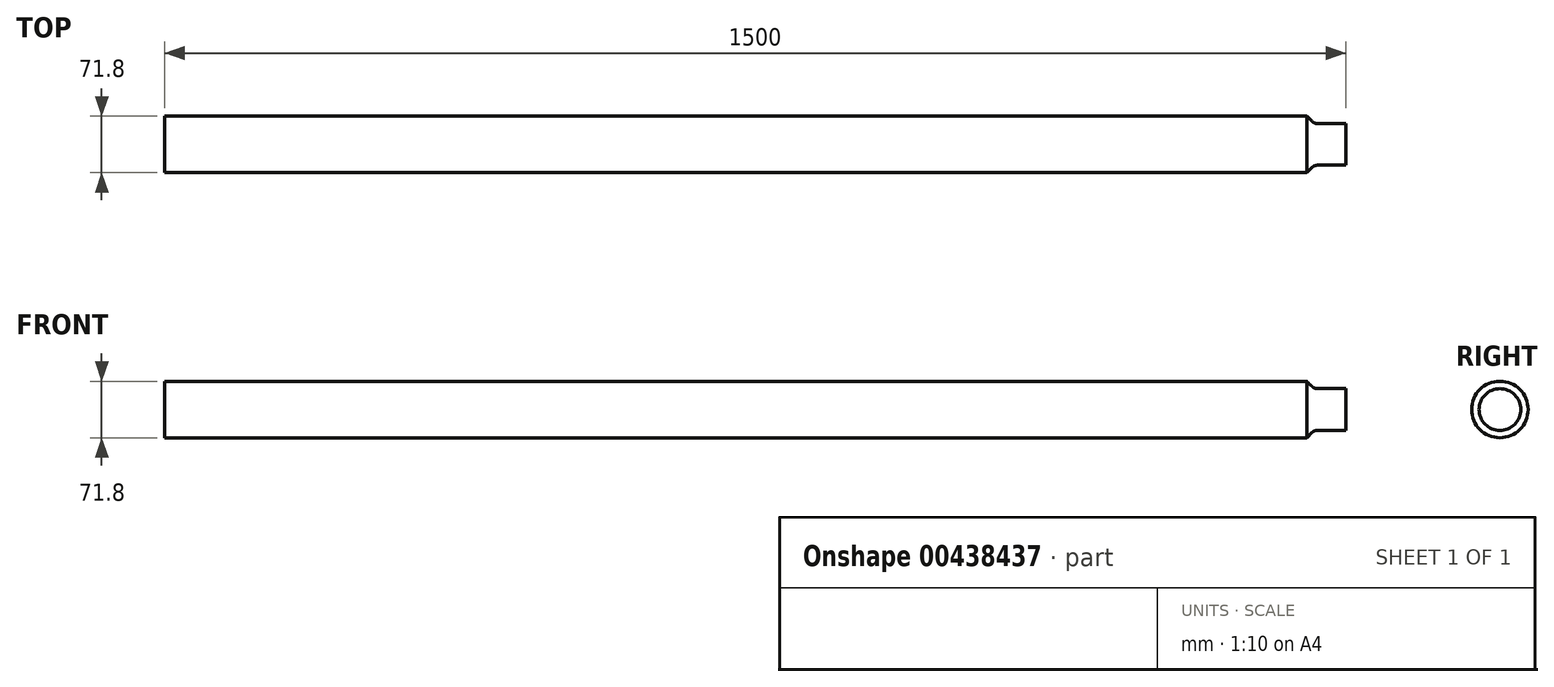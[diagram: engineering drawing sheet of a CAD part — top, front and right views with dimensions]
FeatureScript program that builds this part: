
annotation { "Feature Type Name" : "Feature", "Feature Type Description" : "" }
export const myFeature = defineFeature(function(context is Context, id is Id, definition is map)
    precondition{}
    {
        {
            var Q0;
            Q0=qCreatedBy(makeId("Front.planeOp"),FACE);
            var sketch = newSketch(context, id + "F0", { "sketchPlane" : qUnion([Q0])});
            skLineSegment(sketch, "E0.bottom", {"start": v(0, 35.9) * mm, "end": v(1450.6, 35.9) * mm});
            skLineSegment(sketch, "E0.top", {"start": v(0, 0) * mm, "end": v(1500, 0) * mm});
            skLineSegment(sketch, "E0.left", {"start": v(0, 35.9) * mm, "end": v(0, 0) * mm});
            skLineSegment(sketch, "E1.bottom", {"start": v(0, 24.08) * mm, "end": v(0, 24.08) * mm});
            skLineSegment(sketch, "E1.top", {"start": v(0, 35.9) * mm, "end": v(0, 35.9) * mm});
            skLineSegment(sketch, "E1.left", {"start": v(0, 35.9) * mm, "end": v(0, 24.08) * mm});
            skLineSegment(sketch, "E1.right", {"start": v(0, 35.9) * mm, "end": v(0, 24.08) * mm});
            skLineSegment(sketch, "E2", {"start": v(1460, 26.5) * mm, "end": v(1500, 26.5) * mm});
            skLineSegment(sketch, "E3", {"start": v(1500, 26.5) * mm, "end": v(1500, 0) * mm});
            skLineSegment(sketch, "E4", {"start": v(1460, 26.5) * mm, "end": v(1450.6, 35.9) * mm});
            skPoint(sketch, "E5.end.orphan", {"position": v(1500, 26.5) * mm});
            skSolve(sketch);
        }
        {
            var Q0;
            Q0=makeQuery(id+"F0.imprint","IMPRINT",FACE,{"disambiguationData":[TD([[makeQuery(id+"F0.imprint","IMPRINT",EDGE,{"derivedFrom":sQuery(id+"F0.wireOp",EDGE,"E0.bottom")}),-1.0]])]});
            var Q1;
            Q1=sQuery(id+"F0.wireOp",EDGE,"E0.bottom");
            var Q2;
            Q2=sQuery(id+"F0.wireOp",EDGE,"E0.top");
            var Q3;
            Q3=sQuery(id+"F0.wireOp",EDGE,"E0.top");
            revolve(context, id + "F1", {"entities" : qUnion([Q0]), "surfaceEntities" : qUnion([Q1, Q2]), "axis" : qUnion([Q3]), "revolveType" : RevolveType.SYMMETRIC, "angle" : 360 * degree});
        }
        {
            var Q0;
            Q0=makeQuery(id+"F1.opRevolve","SWEPT_EDGE",EDGE,{"disambiguationData":[OSD([sQuery(id+"F0.wireOp",EDGE,"E2"),sQuery(id+"F0.wireOp",EDGE,"E4")])]});
            fillet(context, id + "F2", {"entities" : qUnion([Q0]), "radius" : 10 * mm, "tangentPropagation" : true, "allowEdgeOverflow" : false});
        }
    });
